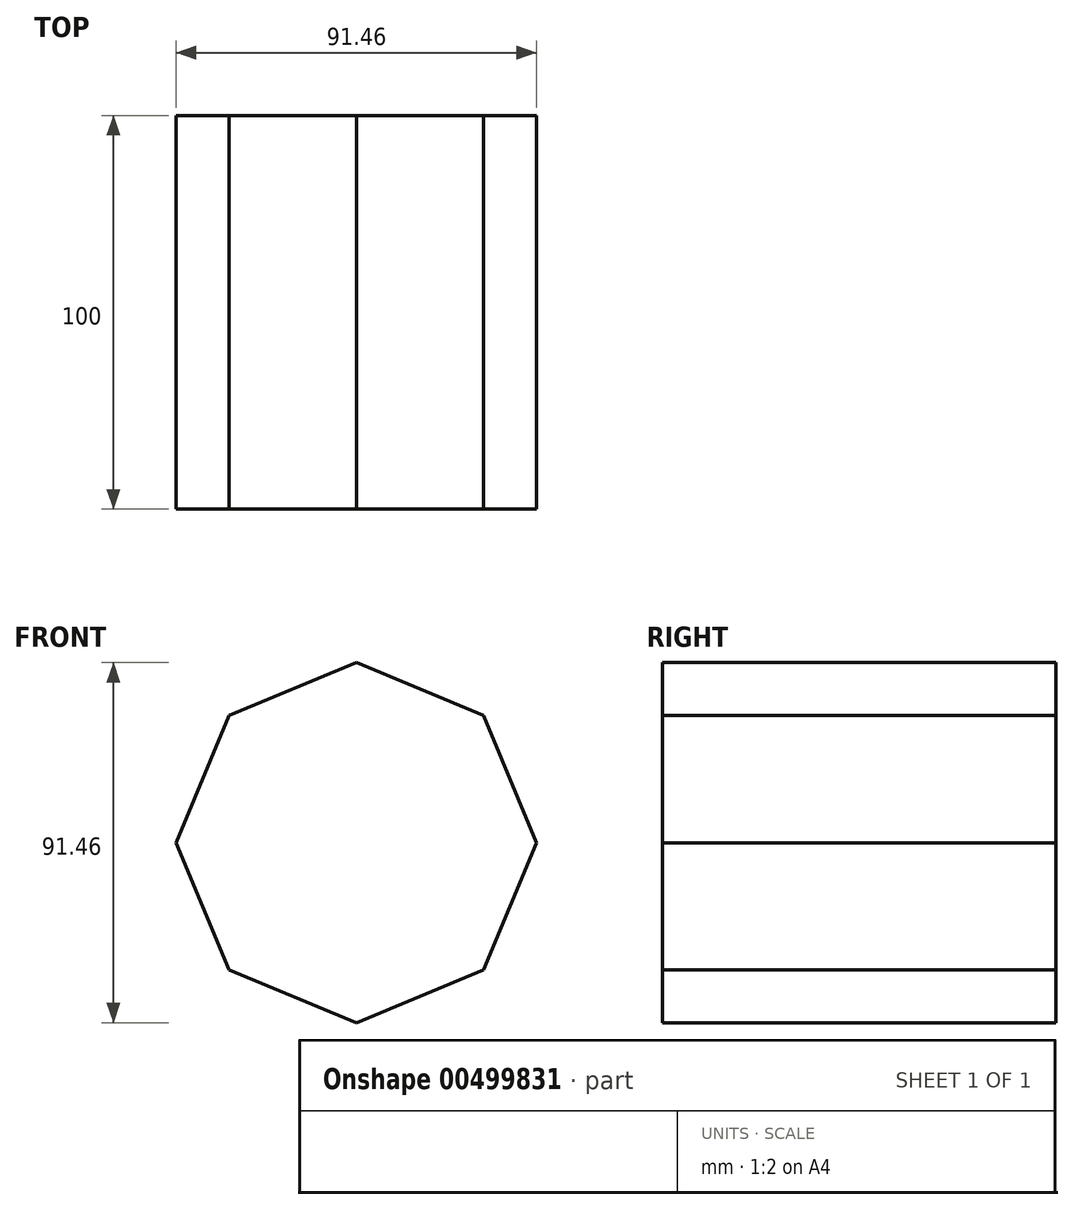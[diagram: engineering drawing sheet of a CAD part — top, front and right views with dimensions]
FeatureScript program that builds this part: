
annotation { "Feature Type Name" : "Feature", "Feature Type Description" : "" }
export const myFeature = defineFeature(function(context is Context, id is Id, definition is map)
    precondition{}
    {
        {
            var Q0;
            Q0=qCreatedBy(makeId("Front.planeOp"),FACE);
            var sketch = newSketch(context, id + "F0", { "sketchPlane" : qUnion([Q0])});
            skCircle(sketch, "E0.cCircle", {"center": v(0, 0) * mm, "radius": 42.25 * mm, "construction": true});
            skLineSegment(sketch, "E0.0", {"start": v(0, 45.73) * mm, "end": v(32.34, 32.34) * mm});
            skLineSegment(sketch, "E0.1", {"start": v(32.34, 32.34) * mm, "end": v(45.73, 0) * mm});
            skLineSegment(sketch, "E0.2", {"start": v(45.73, 0) * mm, "end": v(32.34, -32.34) * mm});
            skLineSegment(sketch, "E0.3", {"start": v(32.34, -32.34) * mm, "end": v(0, -45.73) * mm});
            skLineSegment(sketch, "E0.4", {"start": v(0, -45.73) * mm, "end": v(-32.34, -32.34) * mm});
            skLineSegment(sketch, "E0.5", {"start": v(-32.34, -32.34) * mm, "end": v(-45.73, 0) * mm});
            skLineSegment(sketch, "E0.6", {"start": v(-45.73, 0) * mm, "end": v(-32.34, 32.34) * mm});
            skLineSegment(sketch, "E0.7", {"start": v(-32.34, 32.34) * mm, "end": v(0, 45.73) * mm});
            skPoint(sketch, "E0.0.midPoint", {"position": v(16.17, 39.03) * mm});
            skSolve(sketch);
        }
        {
            var Q0;
            Q0 = qSketchRegion(id + "F0", true);
            extrude(context, id + "F1", {"entities" : qUnion([Q0]), "depth" : 100 * mm, "symmetric" : true});
        }
    });
